# Revit family: UNB_Multisuite_E1318_BIM_DE
name_source: partatom
category: Plumbing Fixtures
revit_build: Autodesk Revit MEP 2016 (Build: 20161004_0715(x64)
units: mm (PartAtom-declared; Revit-internal decimal feet)

## family parameters
Always vertical = No
Cut with Voids When Loaded = No
OmniClass Number = 23.45.05.21.11.11
OmniClass Title = Water Operated Water Closets
Part Type = Normal
Room Calculation Point = No
Round Connector Dimension = Use Diameter
Shared = No
Work Plane-Based = No

## types (1)
- E131801 REVO seat & cover, slow close
    Accessories = www.idealstandard.de\ersatzteile
    AreaUnits = millimeters
    AssetType = Fixed
    BIMObjectName = ISI_IdealStandard_WcSeatsAndCovers_Connect_E131801
    BIMobject category = Toilet Seats
    BOSUseNativeGeometries = 1
    BarCode = 0
    Brand = Ideal Standard
    Brand url = http://www.idealstandard.co.uk
    CodePerformance = 0
    Color = White
    ConnectionType = Plumbing
    Cost = 0 $
    CurrencyUnit = €
    CurrentRevision = 1
    Date of publishing = 2017_11_20
    Description = E131801 REVO seat & cover, slow close
    DurationUnit = year
    EAN code = 0
    Edition number = 1
    ExpectedLife = 25
    Features = REVO seat & cover, slow close
    Finish = White
    IFC Classification = Slab
    IfcExportAs = IfcSanitaryTerminalType
    IfcExportType = TOILETPANS
    Installation instructions = http://www.idealstandard.de
    InstallationInstructions = www.idealstandard.de\produkte
    LinearUnits = millimeters
    MainColor = White
    Manufacturer name = Ideal Standard
    ManufacturerURL = www.idealstandard.com
    Material = Duroplast
    Model = E131801
    ModelNumber = E131801
    ModelReference = E131801 REVO seat & cover, slow close
    NBS Reference Code = 35-93-95
    NBS Reference Description = Wc Seats And Covers
    Name = WcSeatsAndCovers_Connect_E131801_IdealStandard
    NettWeight = 0
    Nominal height = 0
    Nominal width = 0
    NominalDepth = 446 mm  [stored 1.46325 ft]
    NominalHeight = 41 mm
    NominalLength = 446 mm  [stored 1.46325 ft]
    NominalWidth = 365 mm
    OmniClass Code = 23-31 19 00
    OmniClass Description = Toilets
    PanColor = White
    PanMaterial = Duroplast
    Product Guid = 59151ad2-7c25-46f4-a1ff-3a653c4b2da2
    Product SKU = E1318
    Product data url = https://bimobject.com
    Product family = CONNECT
    Product group = Seat & Cover
    Product name = REVO seat & cover, slow close
    Product url = http://www.idealstandard.de
    ProductInformation = www.idealstandard.de/produkte
    QR code = http://bimobject.com
    Shape = Sculptured
    Size = 365x446x41 mm
    Space = Internal
    SpareParts = www.idealstandard.de/ersatzteile
    SpilloverLevel = 0 mm  [stored 0 ft]
    Technical description = http://www.idealstandard.de
    ToiletType = WashDown
    URL = http://www.idealstandard.de
    Uniclass 1.4 Code = L7216
    Uniclass 1.4 Description = Toilets
    Uniclass 2.0 Code = PR-35-93-95
    Uniclass 2.0 Description = Wc Seats And Covers
    Uniclass 2015 Code = Pr_40_20_93_95
    Uniclass 2015 Name = WC seats and covers
    Uniclass2015Code = Pr_40_20_93_95
    Uniclass2015Title = WC seats and covers
    Uniclass2015Version = Products v1.1
    Version = 1
    VolumeUnits = Litres
    Weight Net (Kg) = 0

note: [stored X ft] marks values corroborated as IEEE doubles in the binary element streams (Revit-internal decimal feet)

## geometry (parser evidence)
native form markers: Blend x4, Sweep x1
no freeform markers — native parametric forms only
